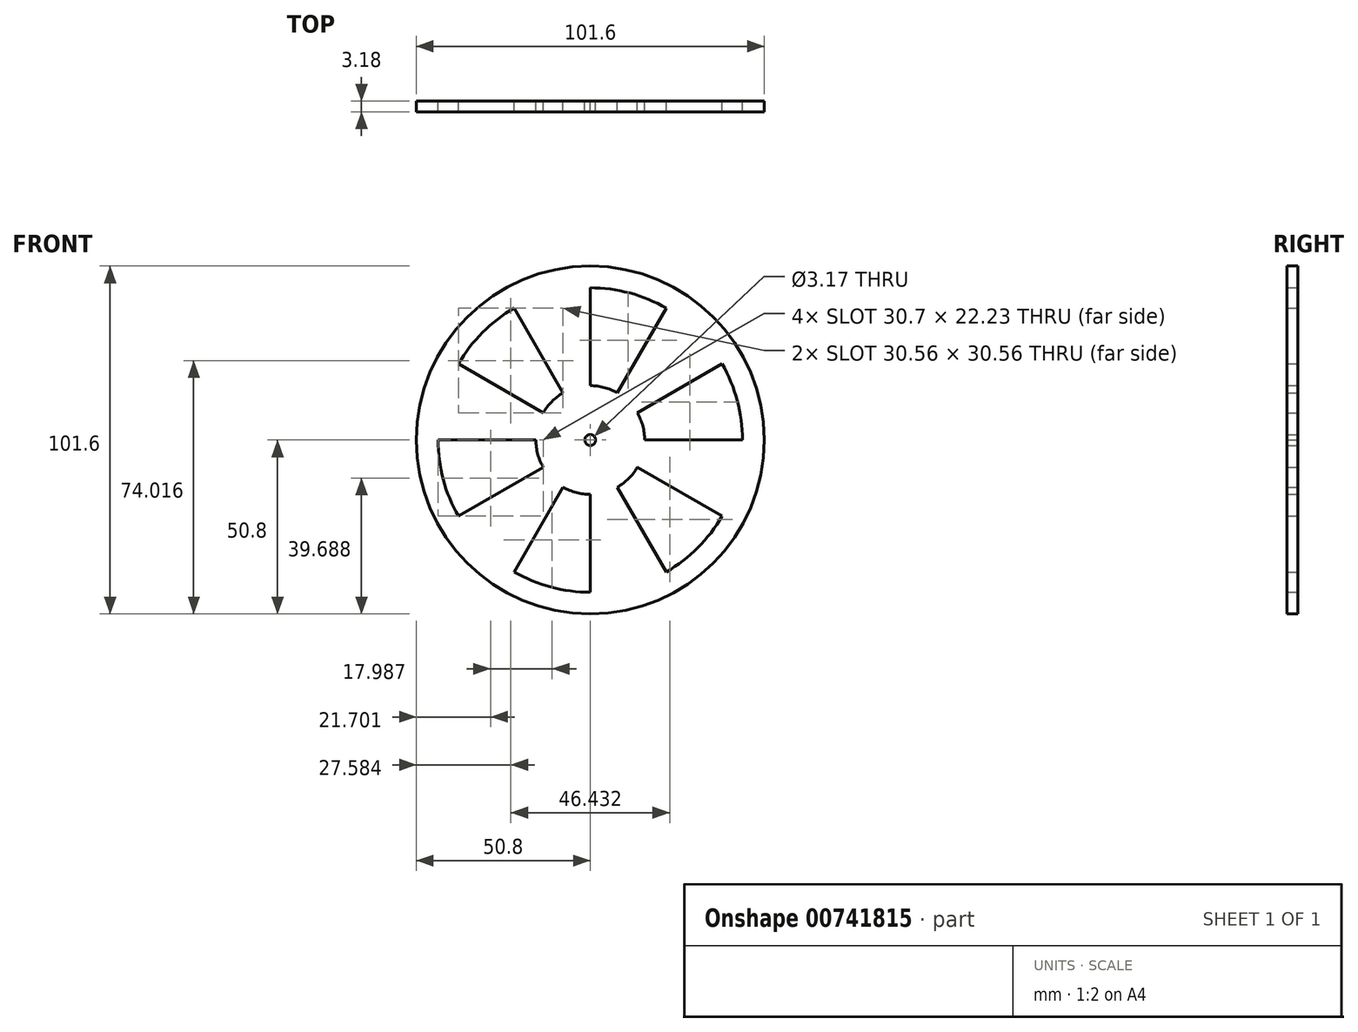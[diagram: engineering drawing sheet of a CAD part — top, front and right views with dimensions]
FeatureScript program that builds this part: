
annotation { "Feature Type Name" : "Feature", "Feature Type Description" : "" }
export const myFeature = defineFeature(function(context is Context, id is Id, definition is map)
    precondition{}
    {
        {
            var Q0;
            Q0=qCreatedBy(makeId("Front.planeOp"),FACE);
            var sketch = newSketch(context, id + "F0", { "sketchPlane" : qUnion([Q0])});
            skCircle(sketch, "E0", {"center": v(0, 0) * mm, "radius": 50.8 * mm});
            skCircle(sketch, "E1", {"center": v(0, 0) * mm, "radius": 1.59 * mm});
            skArc(sketch, "E2", {"start": v(-22.22, 38.5) * mm, "mid": v(-31.43, 31.43) * mm, "end": v(-38.5, 22.23) * mm});
            skLineSegment(sketch, "E3", {"start": v(0, 44.45) * mm, "end": v(0, 15.88) * mm});
            skLineSegment(sketch, "E4", {"start": v(-44.45, 0) * mm, "end": v(-15.88, 0) * mm});
            skLineSegment(sketch, "E5", {"start": v(0, 0) * mm, "end": v(0.8, 1.37) * mm});
            skLineSegment(sketch, "E6", {"start": v(0, 0) * mm, "end": v(1.37, 0.8) * mm});
            skLineSegment(sketch, "E7", {"start": v(0, 0) * mm, "end": v(1.37, -0.8) * mm});
            skLineSegment(sketch, "E8", {"start": v(0, 0) * mm, "end": v(0.8, -1.37) * mm});
            skLineSegment(sketch, "E9.MirrorCS", {"start": v(0, 0) * mm, "end": v(-0.8, 1.37) * mm});
            skLineSegment(sketch, "E10.MirrorCS", {"start": v(0, 0) * mm, "end": v(-1.37, 0.8) * mm});
            skLineSegment(sketch, "E11.MirrorCS", {"start": v(0, 0) * mm, "end": v(-1.37, -0.8) * mm});
            skLineSegment(sketch, "E12.MirrorCS", {"start": v(0, 0) * mm, "end": v(-0.8, -1.37) * mm});
            skArc(sketch, "E13.trimOffspring", {"start": v(22.22, 38.5) * mm, "mid": v(11.5, 42.94) * mm, "end": v(0, 44.45) * mm});
            skArc(sketch, "E14.trimOffspring", {"start": v(44.45, 0) * mm, "mid": v(42.94, 11.5) * mm, "end": v(38.5, 22.23) * mm});
            skArc(sketch, "E15.trimOffspring", {"start": v(22.23, -38.5) * mm, "mid": v(31.43, -31.43) * mm, "end": v(38.5, -22.22) * mm});
            skArc(sketch, "E16.trimOffspring", {"start": v(-22.23, -38.5) * mm, "mid": v(-11.5, -42.94) * mm, "end": v(0, -44.45) * mm});
            skArc(sketch, "E17.trimOffspring", {"start": v(-44.45, 0) * mm, "mid": v(-42.94, -11.5) * mm, "end": v(-38.5, -22.22) * mm});
            skCircle(sketch, "E18", {"center": v(0, 0) * mm, "radius": 15.88 * mm});
            skLineSegment(sketch, "E19.trimOffspring", {"start": v(-13.75, 7.94) * mm, "end": v(-38.5, 22.23) * mm});
            skLineSegment(sketch, "E20.trimOffspring", {"start": v(-7.94, 13.75) * mm, "end": v(-22.22, 38.5) * mm});
            skLineSegment(sketch, "E21.trimOffspring", {"start": v(0, 1.59) * mm, "end": v(0, -1.59) * mm});
            skLineSegment(sketch, "E22.trimOffspring", {"start": v(7.94, 13.75) * mm, "end": v(22.22, 38.5) * mm});
            skLineSegment(sketch, "E23.trimOffspring", {"start": v(13.75, 7.94) * mm, "end": v(38.5, 22.23) * mm});
            skLineSegment(sketch, "E24.trimOffspring", {"start": v(13.75, -7.94) * mm, "end": v(38.5, -22.22) * mm});
            skLineSegment(sketch, "E25.trimOffspring", {"start": v(7.94, -13.75) * mm, "end": v(22.23, -38.5) * mm});
            skLineSegment(sketch, "E26.trimOffspring", {"start": v(-7.94, -13.75) * mm, "end": v(-22.23, -38.5) * mm});
            skLineSegment(sketch, "E27.trimOffspring", {"start": v(-13.75, -7.94) * mm, "end": v(-38.5, -22.22) * mm});
            skLineSegment(sketch, "E28.trimOffspring", {"start": v(-1.59, 0) * mm, "end": v(1.59, 0) * mm});
            skLineSegment(sketch, "E29.trimOffspring", {"start": v(15.88, 0) * mm, "end": v(44.45, 0) * mm});
            skLineSegment(sketch, "E30.trimOffspring", {"start": v(0, -15.88) * mm, "end": v(0, -44.45) * mm});
            skSolve(sketch);
        }
        {
            var Q0;
            Q0=makeQuery(id+"F0.imprint","IMPRINT",FACE,{"disambiguationData":[TD([[makeQuery(id+"F0.imprint","IMPRINT",EDGE,{"derivedFrom":sQuery(id+"F0.wireOp",EDGE,"E0")}),1.0]])]});
            var Q1;
            {var subQ6=sQuery(id+"F0.wireOp",EDGE,"E1");var subQ16=makeQuery(id+"F0.imprint","INTERSECT",VERTEX,{"derivedFrom":[subQ6,sQuery(id+"F0.wireOp",EDGE,"E6")]});Q1=makeQuery(id+"F0.imprint","IMPRINT",FACE,{"disambiguationData":[TD([[makeQuery(id+"F0.imprint","IMPRINT",EDGE,{"disambiguationData":[TD([[subQ16,1.0]])],"derivedFrom":subQ6}),-1.0]])]});}
            extrude(context, id + "F1", {"entities" : qUnion([Q0, Q1]), "depth" : 3.17 * mm, "offsetDistance" : 25.4 * mm});
        }
    });
